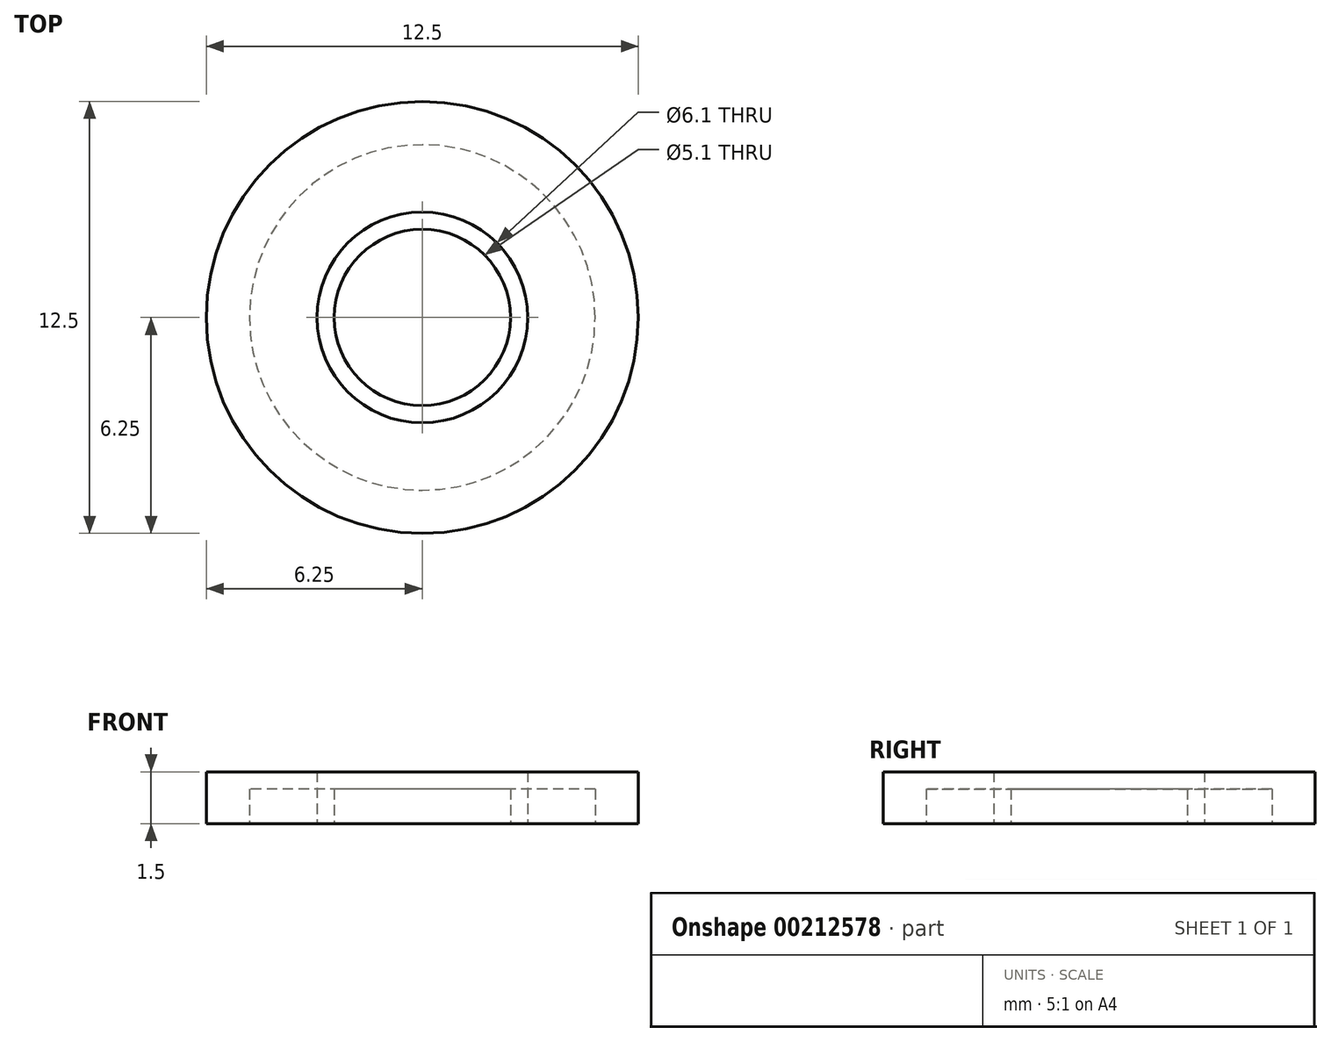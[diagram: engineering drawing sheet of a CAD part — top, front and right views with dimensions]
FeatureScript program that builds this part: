
annotation { "Feature Type Name" : "Feature", "Feature Type Description" : "" }
export const myFeature = defineFeature(function(context is Context, id is Id, definition is map)
    precondition{}
    {
        {
            var Q0;
            Q0=qCreatedBy(makeId("Top.planeOp"),FACE);
            var sketch = newSketch(context, id + "F0", { "sketchPlane" : qUnion([Q0])});
            skCircle(sketch, "E0", {"center": v(0, 0) * mm, "radius": 5 * mm});
            skCircle(sketch, "E1", {"center": v(0, 0) * mm, "radius": 2.55 * mm});
            skSolve(sketch);
        }
        {
            var Q0;
            Q0=makeQuery(id+"F0.imprint","IMPRINT",FACE,{"disambiguationData":[TD([[makeQuery(id+"F0.imprint","IMPRINT",EDGE,{"derivedFrom":sQuery(id+"F0.wireOp",EDGE,"E0")}),1.0]])]});
            extrude(context, id + "F1", {"entities" : qUnion([Q0]), "depth" : 1 * mm, "offsetDistance" : 25 * mm});
        }
        {
            var Q0;
            Q0=qCreatedBy(makeId("Top.planeOp"),FACE);
            var sketch = newSketch(context, id + "F2", { "sketchPlane" : qUnion([Q0])});
            skCircle(sketch, "E2", {"center": v(0, 0) * mm, "radius": 6.25 * mm});
            skCircle(sketch, "E3", {"center": v(0, 0) * mm, "radius": 3.05 * mm});
            skSolve(sketch);
        }
        {
            var Q0;
            Q0=makeQuery(id+"F2.imprint","IMPRINT",FACE,{"disambiguationData":[TD([[makeQuery(id+"F2.imprint","IMPRINT",EDGE,{"derivedFrom":sQuery(id+"F2.wireOp",EDGE,"E2")}),1.0]])]});
            extrude(context, id + "F3", {"entities" : qUnion([Q0]), "depth" : 1.5 * mm, "offsetDistance" : 25 * mm});
        }
    });
